# Revit family: Diverter_Rough_Valve-DXV-D35000420.191
name_source: partatom
category: Plumbing Fixtures
revit_build: Autodesk Revit 2014 (Build: 20130308_1515(x64)
units: mm (PartAtom-declared; Revit-internal decimal feet)

## types (1)
- D35000420.191
    Assembly Code = D2020300
    CW Connection = Yes
    CWFU = 3
    Default Elevation = 40"
    Description = 3/2 Port Diverter Rough Valve
    Finish = Cast Brass-DXV-Unfinished
    HW Connection = Yes
    HWFU = 3
    Height = 3 1/8"
    Installation Type = In-Wall
    Manufacturer = DXV
    Material = Cast Brass-DXV-Unfinished
    Model = D35000420.191
    Price = Prices may vary. Please consult Manufacturer Representative for most up-to-date price list.
    Product Documentation Link = https://dxv01.blob.core.windows.net
    Product Page URL = https://www.dxv.com
    Revised Date = 12/04/2017
    Tempered Water Connection Diameter = 1/2"
    URL = https://www.dxv.com
    Vent Connection = No
    WFU = 4
    Warranty Documentation Link = https://www.dxv.com
    Waste Connection = No
    Width = 3 1/8"

## geometry (parser evidence)
native form markers: Sweep x3
no freeform markers — native parametric forms only
